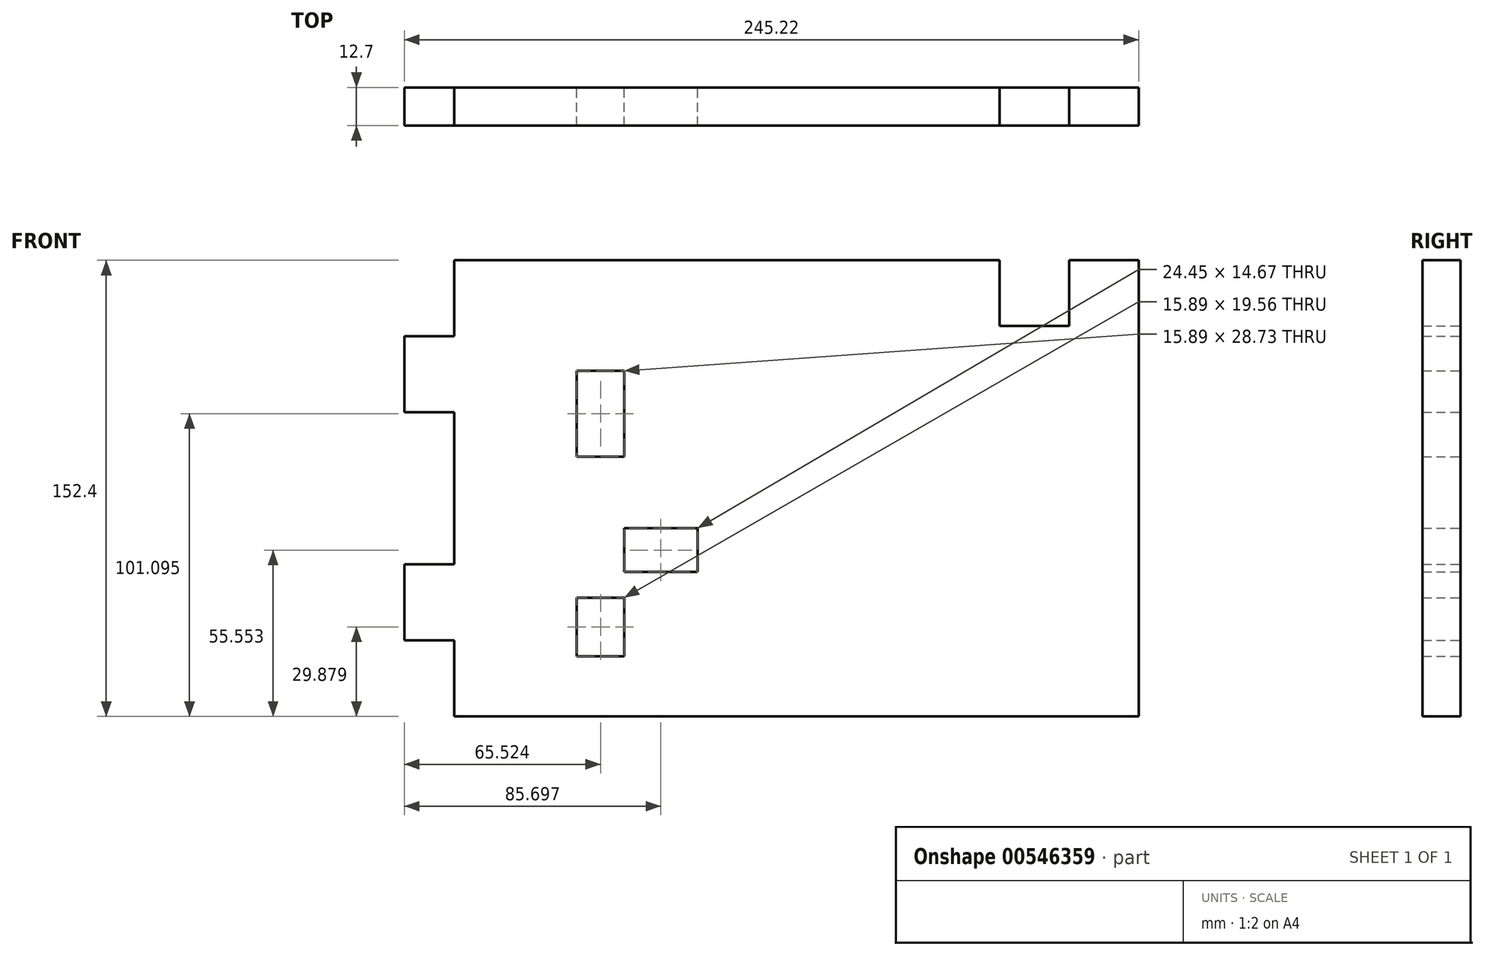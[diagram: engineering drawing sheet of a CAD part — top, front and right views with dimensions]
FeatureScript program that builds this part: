
annotation { "Feature Type Name" : "Feature", "Feature Type Description" : "" }
export const myFeature = defineFeature(function(context is Context, id is Id, definition is map)
    precondition{}
    {
        {
            var Q0;
            Q0=qCreatedBy(makeId("Front.planeOp"),FACE);
            var sketch = newSketch(context, id + "F0", { "sketchPlane" : qUnion([Q0])});
            skLineSegment(sketch, "E0.bottom", {"start": v(-105.99, 76.2) * mm, "end": v(76.18, 76.2) * mm});
            skLineSegment(sketch, "E0.top", {"start": v(-105.99, -76.2) * mm, "end": v(122.61, -76.2) * mm});
            skLineSegment(sketch, "E0.left", {"start": v(-122.61, 50.8) * mm, "end": v(-122.61, 25.4) * mm});
            skLineSegment(sketch, "E0.right", {"start": v(122.61, 76.2) * mm, "end": v(122.61, -76.2) * mm});
            skPoint(sketch, "E0.middle", {"position": v(0, 0) * mm});
            skLineSegment(sketch, "E1", {"start": v(-105.99, 76.2) * mm, "end": v(-105.99, 50.8) * mm});
            skLineSegment(sketch, "E2", {"start": v(-105.99, 50.8) * mm, "end": v(-122.61, 50.8) * mm});
            skLineSegment(sketch, "E3", {"start": v(-122.61, 25.4) * mm, "end": v(-105.99, 25.4) * mm});
            skLineSegment(sketch, "E4", {"start": v(-105.99, 25.4) * mm, "end": v(-105.99, -25.4) * mm});
            skLineSegment(sketch, "E5", {"start": v(-105.99, -25.4) * mm, "end": v(-122.61, -25.4) * mm});
            skLineSegment(sketch, "E6", {"start": v(-122.61, -25.4) * mm, "end": v(-122.61, -50.8) * mm});
            skLineSegment(sketch, "E7", {"start": v(-122.61, -50.8) * mm, "end": v(-105.99, -50.8) * mm});
            skLineSegment(sketch, "E8", {"start": v(-105.99, -50.8) * mm, "end": v(-105.99, -76.2) * mm});
            skLineSegment(sketch, "E9", {"start": v(76.18, 76.2) * mm, "end": v(76.18, 54.3) * mm});
            skLineSegment(sketch, "E10", {"start": v(76.18, 54.3) * mm, "end": v(99.4, 54.3) * mm});
            skLineSegment(sketch, "E11", {"start": v(99.4, 54.3) * mm, "end": v(99.4, 76.2) * mm});
            skLineSegment(sketch, "E12", {"start": v(-65.03, 39.26) * mm, "end": v(-49.14, 39.26) * mm});
            skLineSegment(sketch, "E13", {"start": v(-49.14, 39.26) * mm, "end": v(-49.14, 10.53) * mm});
            skLineSegment(sketch, "E14", {"start": v(-49.14, 10.53) * mm, "end": v(-65.03, 10.53) * mm});
            skLineSegment(sketch, "E15", {"start": v(-65.03, 10.53) * mm, "end": v(-65.03, 39.26) * mm});
            skLineSegment(sketch, "E16", {"start": v(-65.03, -36.54) * mm, "end": v(-49.14, -36.54) * mm});
            skLineSegment(sketch, "E17", {"start": v(-49.14, -36.54) * mm, "end": v(-49.14, -56.1) * mm});
            skLineSegment(sketch, "E18", {"start": v(-49.14, -56.1) * mm, "end": v(-65.03, -56.1) * mm});
            skLineSegment(sketch, "E19", {"start": v(-65.03, -56.1) * mm, "end": v(-65.03, -36.54) * mm});
            skLineSegment(sketch, "E20", {"start": v(-49.14, -27.98) * mm, "end": v(-24.69, -27.98) * mm});
            skLineSegment(sketch, "E21", {"start": v(-24.69, -27.98) * mm, "end": v(-24.69, -13.31) * mm});
            skLineSegment(sketch, "E22", {"start": v(-24.69, -13.31) * mm, "end": v(-49.14, -13.31) * mm});
            skLineSegment(sketch, "E23", {"start": v(-49.14, -13.31) * mm, "end": v(-49.14, -27.98) * mm});
            skLineSegment(sketch, "E24.trimOffspring", {"start": v(99.4, 76.2) * mm, "end": v(122.61, 76.2) * mm});
            skPoint(sketch, "E25.orphan", {"position": v(-122.61, 76.2) * mm});
            skPoint(sketch, "E26.orphan", {"position": v(-122.61, -76.2) * mm});
            skSolve(sketch);
        }
        {
            var Q0;
            Q0 = qSketchRegion(id + "F0", true);
            extrude(context, id + "F1", {"entities" : qUnion([Q0]), "endBound" : BoundingType.SYMMETRIC, "depth" : 12.7 * mm, "offsetDistance" : 25.4 * mm});
        }
    });
